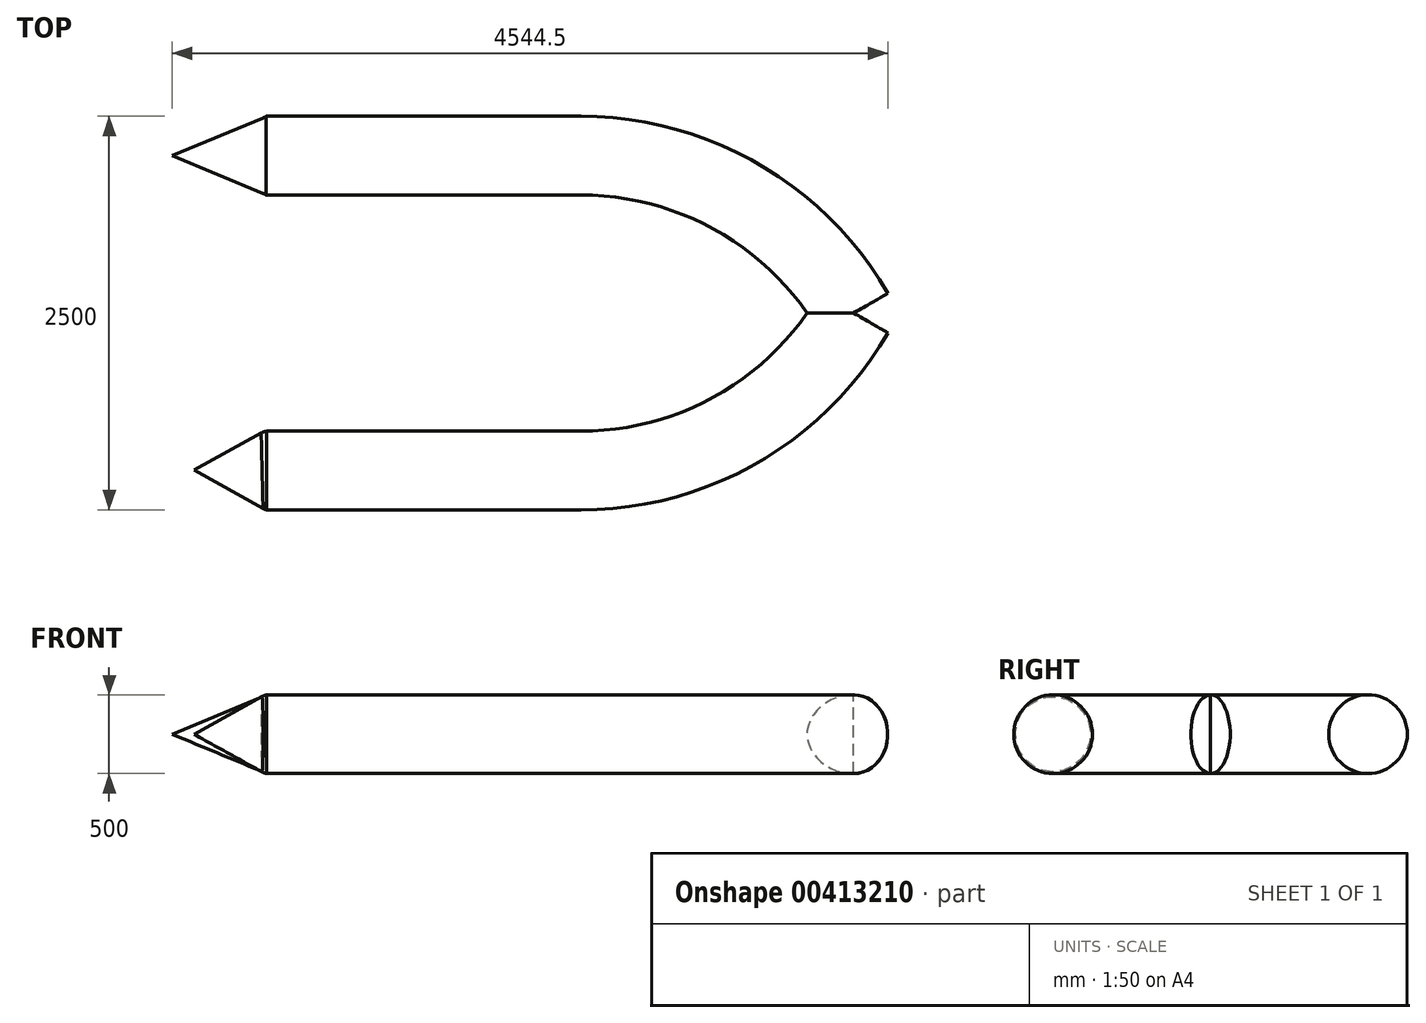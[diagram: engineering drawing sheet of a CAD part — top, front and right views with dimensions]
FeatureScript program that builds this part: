
annotation { "Feature Type Name" : "Feature", "Feature Type Description" : "" }
export const myFeature = defineFeature(function(context is Context, id is Id, definition is map)
    precondition{}
    {
        {
            var Q0;
            Q0=qCreatedBy(makeId("Top.planeOp"),FACE);
            var sketch = newSketch(context, id + "F0", { "sketchPlane" : qUnion([Q0])});
            skLineSegment(sketch, "E0", {"start": v(-4.06, 1000) * mm, "end": v(1995.94, 1000) * mm});
            skArc(sketch, "E1", {"start": v(1995.94, 1000) * mm, "mid": v(2995.94, 732.05) * mm, "end": v(3728, 0) * mm});
            skSolve(sketch);
        }
        {
            var Q0;
            Q0=qCreatedBy(makeId("Right.planeOp"),FACE);
            var sketch = newSketch(context, id + "F1", { "sketchPlane" : qUnion([Q0])});
            skCircle(sketch, "E2", {"center": v(1000, 0) * mm, "radius": 250 * mm});
            skSolve(sketch);
        }
        {
            var Q0;
            Q0=makeQuery(id+"F1.imprint","IMPRINT",FACE,{"disambiguationData":[TD([[makeQuery(id+"F1.imprint","IMPRINT",EDGE,{"derivedFrom":sQuery(id+"F1.wireOp",EDGE,"E2")}),1.0]])]});
            var Q1;
            Q1=sQuery(id+"F0.wireOp",EDGE,"e41bee1b-3aa3-4e08-bbd5-2938b15bb243");
            var Q2;
            Q2=sQuery(id+"F0.wireOp",EDGE,"e41bee1b-3aa3-4e08-bbd5-2938b15bb243");
            var Q3;
            Q3=sQuery(id+"F0.wireOp",EDGE,"E0");
            var Q4;
            Q4=sQuery(id+"F0.wireOp",EDGE,"E1");
            sweep(context, id + "F2", {"profiles" : qUnion([Q0]), "surfaceProfiles" : qUnion([Q1]), "path" : qUnion([Q2, Q3, Q4])});
        }
        {
            var Q0;
            Q0=makeQuery(id+"F2.opSweep","SWEPT_BODY",BODY,{"disambiguationData":[OSD([sQuery(id+"F0.wireOp",EDGE,"c231d90d-ce99-4874-8226-b017b3ed26ba"),sQuery(id+"F1.wireOp",EDGE,"E2")])]});
            var Q1;
            Q1=qCreatedBy(makeId("Front.planeOp"),FACE);
            mirror(context, id + "F3", {"operationType" : NewBodyOperationType.ADD, "entities" : qUnion([Q0]), "mirrorPlane" : qUnion([Q1])});
        }
        {
            var Q0;
            Q0=makeQuery(id+"F2.opSweep","CAP_FACE",FACE,{"disambiguationData":[OSD([sQuery(id+"F0.wireOp",VERTEX,"E1.end"),sQuery(id+"F1.wireOp",EDGE,"E2")])],"isStart":false});
            var sketch = newSketch(context, id + "F4", { "sketchPlane" : qUnion([Q0])});
            skLineSegment(sketch, "E3.0.0", {"start": v(3235.56, 249.9) * mm, "end": v(3235.56, -249.9) * mm});
            skArc(sketch, "E3.0.1", {"start": v(3235.56, -249.9) * mm, "mid": v(3478.54, 0) * mm, "end": v(3235.56, 249.9) * mm});
            skSolve(sketch);
        }
        {
            var Q0;
            Q0=makeQuery(id+"F4.imprint","IMPRINT",FACE,{"disambiguationData":[TD([[makeQuery(id+"F4.imprint","IMPRINT",EDGE,{"derivedFrom":sQuery(id+"F4.wireOp",EDGE,"E3.0.0")}),-1.0]])]});
            var Q1;
            Q1=sQuery(id+"F4.wireOp",EDGE,"E3.0.0");
            var Q2;
            Q2=sQuery(id+"F4.wireOp",EDGE,"E3.0.0");
            revolve(context, id + "F5", {"operationType" : NewBodyOperationType.ADD, "entities" : qUnion([Q0]), "surfaceEntities" : qUnion([Q1]), "axis" : qUnion([Q2]), "revolveType" : RevolveType.ONE_DIRECTION, "angle" : 60 * degree});
        }
        {
            var Q0;
            Q0=qCreatedBy(makeId("Top.planeOp"),FACE);
            cPlane(context, id + "F6", {"entities" : qUnion([Q0]), "cplaneType" : CPlaneType.OFFSET, "offset" : 250 * mm, "oppositeDirection" : true, "width" : 150 * mm, "height" : 150 * mm});
        }
        {
            var Q0;
            Q0=qCreatedBy(makeId("Front.planeOp"),FACE);
            var sketch = newSketch(context, id + "F7", { "sketchPlane" : qUnion([Q0])});
            skFitSpline(sketch, "E4", {"points": [v(3728.4, -249.5) * mm, v(2097.12, -777.96) * mm, v(80.28, -752.14) * mm, v(0, -250) * mm], "startDerivative": vector(-5711.08, -3848.17) * mm, "endDerivative": vector(-428.84, 4369.42) * mm});
            skSolve(sketch);
        }
        {
            var Q0;
            Q0=qCreatedBy(id+"F6.planeOp",FACE);
            var sketch = newSketch(context, id + "F8", { "sketchPlane" : qUnion([Q0])});
            skLineSegment(sketch, "E5.0", {"start": v(-4.06, 1000) * mm, "end": v(1995.94, 1000) * mm, "construction": true});
            skArc(sketch, "E5.1", {"start": v(1995.94, 1000) * mm, "mid": v(2995.94, 732.05) * mm, "end": v(3728, 0) * mm, "construction": true});
            skFitSpline(sketch, "E6", {"points": [v(-4.06, 1000) * mm, v(1995.94, 1000) * mm, v(3728, 0) * mm], "startDerivative": vector(6000, 0) * mm, "endDerivative": vector(3028.75, -5025.45) * mm});
            skSolve(sketch);
        }
        {
            var Q0;
            Q0=sQuery(id+"F8.wireOp",EDGE,"E6");
            var Q1;
            Q1=sQuery(id+"F7.wireOp",EDGE,"E4");
            loft(context, id + "F9", {"bodyType" : ToolBodyType.SURFACE, "wireProfilesArray" : [{ "wireProfileEntities" : qUnion([Q0]) }, { "wireProfileEntities" : qUnion([Q1]) }]});
        }
        {
            var Q0;
            Q0=qCreatedBy(makeId("Top.planeOp"),FACE);
            var sketch = newSketch(context, id + "F10", { "sketchPlane" : qUnion([Q0])});
            skLineSegment(sketch, "E7", {"start": v(0, 1000) * mm, "end": v(-600, 1000) * mm, "construction": true});
            skLineSegment(sketch, "E8.MirrorCS", {"start": v(0, -1008.93) * mm, "end": v(-600, -1008.93) * mm, "construction": true});
            skLineSegment(sketch, "E9", {"start": v(-600, 1000) * mm, "end": v(0, 750.71) * mm});
            skLineSegment(sketch, "E10", {"start": v(0, 750.71) * mm, "end": v(0, 1000) * mm});
            skLineSegment(sketch, "E11", {"start": v(0, 1000) * mm, "end": v(-600, 1000) * mm});
            skSolve(sketch);
        }
        {
            var Q0;
            Q0=makeQuery(id+"F9.opLoft","SWEPT_BODY",BODY,{"disambiguationData":[OSD([sQuery(id+"F7.wireOp",EDGE,"E4"),sQuery(id+"F8.wireOp",EDGE,"E6")])]});
            var Q1;
            Q1=qCreatedBy(makeId("Front.planeOp"),FACE);
            mirror(context, id + "F11", {"entities" : qUnion([Q0]), "mirrorPlane" : qUnion([Q1])});
        }
        {
            var Q0;
            Q0 = qSketchRegion(id + "F10", true);
            var Q1;
            Q1=sQuery(id+"F10.wireOp",EDGE,"E11");
            revolve(context, id + "F12", {"operationType" : NewBodyOperationType.ADD, "entities" : qUnion([Q0]), "axis" : qUnion([Q1]), "revolveType" : RevolveType.FULL});
        }
        {
            var Q0;
            Q0=qCreatedBy(makeId("Top.planeOp"),FACE);
            var sketch = newSketch(context, id + "F13", { "sketchPlane" : qUnion([Q0])});
            skLineSegment(sketch, "E12", {"start": v(0, -997.85) * mm, "end": v(-462.14, -997.85) * mm});
            skLineSegment(sketch, "E13", {"start": v(-462.14, -997.85) * mm, "end": v(0, -742.16) * mm});
            skLineSegment(sketch, "E14", {"start": v(-462.14, -997.85) * mm, "end": v(-859.13, -997.85) * mm, "construction": true});
            skLineSegment(sketch, "E15", {"start": v(0, -742.16) * mm, "end": v(0, -997.85) * mm});
            skSolve(sketch);
        }
        {
            var Q0;
            Q0 = qSketchRegion(id + "F13", true);
            var Q1;
            Q1=sQuery(id+"F13.wireOp",EDGE,"E14");
            revolve(context, id + "F14", {"operationType" : NewBodyOperationType.ADD, "entities" : qUnion([Q0]), "axis" : qUnion([Q1]), "revolveType" : RevolveType.FULL});
        }
        {
            var Q0;
            Q0=makeQuery(id+"F14.opRevolve","SWEPT_FACE",FACE,{"disambiguationData":[OSD([sQuery(id+"F13.wireOp",EDGE,"E13")])]});
            var Q1;
            Q1=makeQuery(id+"F12.opRevolve","SWEPT_FACE",FACE,{"disambiguationData":[OSD([sQuery(id+"F10.wireOp",EDGE,"E9")])]});
            fillet(context, id + "F15", {"entities" : qUnion([Q0, Q1]), "radius" : 100 * mm, "allowEdgeOverflow" : false});
        }
    });
